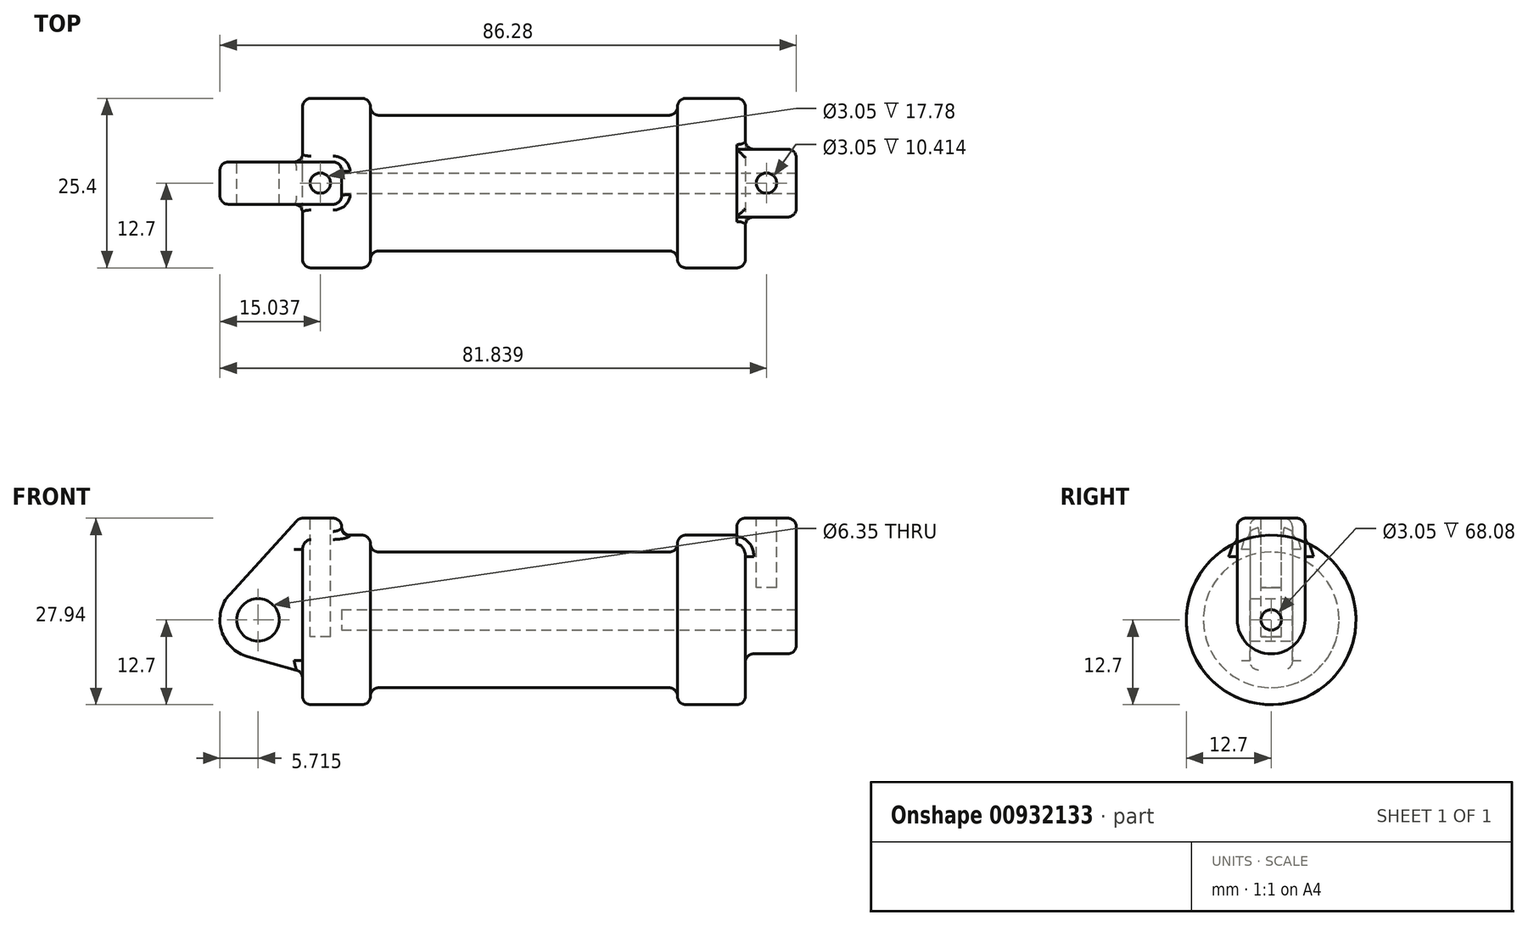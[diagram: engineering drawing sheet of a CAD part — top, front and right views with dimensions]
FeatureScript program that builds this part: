
annotation { "Feature Type Name" : "Feature", "Feature Type Description" : "" }
export const myFeature = defineFeature(function(context is Context, id is Id, definition is map)
    precondition{}
    {
        {
            var Q0;
            Q0=qCreatedBy(makeId("Front.planeOp"),FACE);
            var sketch = newSketch(context, id + "F0", { "sketchPlane" : qUnion([Q0])});
            skLineSegment(sketch, "E0", {"start": v(0, 0) * mm, "end": v(0, 12.7) * mm});
            skLineSegment(sketch, "E1", {"start": v(0, 12.7) * mm, "end": v(10.16, 12.7) * mm});
            skLineSegment(sketch, "E2", {"start": v(10.16, 12.7) * mm, "end": v(10.16, 10.16) * mm});
            skLineSegment(sketch, "E3", {"start": v(10.16, 10.16) * mm, "end": v(56.13, 10.16) * mm});
            skLineSegment(sketch, "E4", {"start": v(56.13, 10.16) * mm, "end": v(56.13, 12.7) * mm});
            skLineSegment(sketch, "E5", {"start": v(56.13, 12.7) * mm, "end": v(66.3, 12.7) * mm});
            skLineSegment(sketch, "E6", {"start": v(66.3, 12.7) * mm, "end": v(66.3, 0) * mm});
            skLineSegment(sketch, "E7", {"start": v(66.3, 0) * mm, "end": v(0, 0) * mm});
            skLineSegment(sketch, "E8", {"start": v(5.84, 15.24) * mm, "end": v(-0.5, 15.24) * mm});
            skLineSegment(sketch, "E9", {"start": v(-0.5, 15.24) * mm, "end": v(-10.88, 3.85) * mm});
            skLineSegment(sketch, "E10", {"start": v(0, 0) * mm, "end": v(-6.65, 0) * mm});
            skCircle(sketch, "E11", {"center": v(-6.65, 0) * mm, "radius": 5.72 * mm});
            skCircle(sketch, "E12", {"center": v(-6.65, 0) * mm, "radius": 3.18 * mm});
            skLineSegment(sketch, "E13", {"start": v(5.84, 15.24) * mm, "end": v(5.84, -9.4) * mm});
            skLineSegment(sketch, "E14", {"start": v(5.84, -9.4) * mm, "end": v(-8.18, -5.5) * mm});
            skLineSegment(sketch, "E15", {"start": v(5.84, 5.08) * mm, "end": v(74.63, 5.08) * mm, "construction": true});
            skSolve(sketch);
        }
        {
            var Q0;
            {var subQ0=sQuery(id+"F0.wireOp",EDGE,"E2");Q0=makeQuery(id+"F0.imprint","IMPRINT",FACE,{"disambiguationData":[TD([[makeQuery(id+"F0.imprint","IMPRINT",EDGE,{"derivedFrom":subQ0}),-1.0]])]});}
            var Q1;
            {var subQ0=sQuery(id+"F0.wireOp",EDGE,"E0");Q1=makeQuery(id+"F0.imprint","IMPRINT",FACE,{"disambiguationData":[TD([[makeQuery(id+"F0.imprint","IMPRINT",EDGE,{"derivedFrom":subQ0}),-1.0]])]});}
            var Q2;
            Q2=sQuery(id+"F0.wireOp",EDGE,"E7");
            revolve(context, id + "F1", {"surfaceOperationType" : NewSurfaceOperationType.NEW, "entities" : qUnion([Q0, Q1]), "axis" : qUnion([Q2]), "revolveType" : RevolveType.FULL});
        }
        {
            var Q0;
            {var subQ1=sQuery(id+"F0.wireOp",EDGE,"E0");Q0=makeQuery(id+"F0.imprint","IMPRINT",FACE,{"disambiguationData":[TD([[makeQuery(id+"F0.imprint","IMPRINT",EDGE,{"derivedFrom":subQ1}),1.0]])]});}
            var Q1;
            {var subQ0=sQuery(id+"F0.wireOp",EDGE,"E0");Q1=makeQuery(id+"F0.imprint","IMPRINT",FACE,{"disambiguationData":[TD([[makeQuery(id+"F0.imprint","IMPRINT",EDGE,{"derivedFrom":subQ0}),-1.0]])]});}
            var Q2;
            {var subQ0=sQuery(id+"F0.wireOp",EDGE,"E14");Q2=makeQuery(id+"F0.imprint","IMPRINT",FACE,{"disambiguationData":[TD([[makeQuery(id+"F0.imprint","IMPRINT",EDGE,{"derivedFrom":subQ0}),-1.0]])]});}
            var Q3;
            {var subQ5=sQuery(id+"F0.wireOp",EDGE,"E12");Q3=makeQuery(id+"F0.imprint","IMPRINT",FACE,{"disambiguationData":[TD([[makeQuery(id+"F0.imprint","IMPRINT",EDGE,{"derivedFrom":subQ5}),-1.0]])]});}
            extrude(context, id + "F2", {"entities" : qUnion([Q0, Q1, Q2, Q3]), "operationType" : NewBodyOperationType.ADD, "endBound" : BoundingType.SYMMETRIC, "depth" : 6.35 * mm, "offsetDistance" : 25.4 * mm});
        }
        {
            var Q0;
            Q0=makeQuery(id+"F1.opRevolve","SWEPT_FACE",FACE,{"disambiguationData":[OSD([sQuery(id+"F0.wireOp",EDGE,"E6")])]});
            var sketch = newSketch(context, id + "F3", { "sketchPlane" : qUnion([Q0])});
            skCircle(sketch, "E16", {"center": v(0, 0) * mm, "radius": 5.08 * mm});
            skCircle(sketch, "E17", {"center": v(0, 0) * mm, "radius": 1.52 * mm});
            skLineSegment(sketch, "E18", {"start": v(5.08, 0) * mm, "end": v(5.08, 15.24) * mm});
            skLineSegment(sketch, "E19", {"start": v(5.08, 15.24) * mm, "end": v(-5.08, 15.24) * mm});
            skLineSegment(sketch, "E20", {"start": v(-5.08, 15.24) * mm, "end": v(-5.08, 0) * mm});
            skSolve(sketch);
        }
        {
            var Q0;
            Q0 = qSketchRegion(id + "F3", true);
            extrude(context, id + "F4", {"entities" : qUnion([Q0]), "oppositeDirection" : true, "depth" : 1.27 * mm, "offsetDistance" : 1.27 * mm, "hasSecondDirection" : true, "secondDirectionOppositeDirection" : false, "secondDirectionDepth" : 7.62 * mm});
        }
        {
            var Q0;
            Q0=makeQuery(id+"F4.opExtrude","SWEPT_BODY",BODY,{"disambiguationData":[OSD([sQuery(id+"F3.wireOp",EDGE,"E16"),sQuery(id+"F3.wireOp",EDGE,"E17"),sQuery(id+"F3.wireOp",EDGE,"E18"),sQuery(id+"F3.wireOp",EDGE,"E19"),sQuery(id+"F3.wireOp",EDGE,"E20")])]});
            var Q1;
            Q1=makeQuery(id+"F1.opRevolve","SWEPT_BODY",BODY,{"disambiguationData":[OSD([sQuery(id+"F0.wireOp",EDGE,"E0"),sQuery(id+"F0.wireOp",EDGE,"E1"),sQuery(id+"F0.wireOp",EDGE,"E2"),sQuery(id+"F0.wireOp",EDGE,"E3"),sQuery(id+"F0.wireOp",EDGE,"E4"),sQuery(id+"F0.wireOp",EDGE,"E5"),sQuery(id+"F0.wireOp",EDGE,"E6"),sQuery(id+"F0.wireOp",EDGE,"E7")])]});
            booleanBodies(context, id + "F5", {"operationType" : BooleanOperationType.UNION, "tools" : qUnion([Q0, Q1])});
        }
        {
            var Q0;
            Q0=makeQuery(id+"F5.opBoolean","SPLIT",FACE,{"disambiguationData":[TD([makeQuery(id+"F4.opExtrude","SWEPT_FACE",FACE,{"disambiguationData":[OSD([sQuery(id+"F3.wireOp",EDGE,"E17")])]})])],"derivedFrom":makeQuery(id+"F1.opRevolve","SWEPT_FACE",FACE,{"disambiguationData":[OSD([sQuery(id+"F0.wireOp",EDGE,"E6")])]})});
            extrude(context, id + "F6", {"entities" : qUnion([Q0]), "operationType" : NewBodyOperationType.REMOVE, "oppositeDirection" : true, "depth" : 60.46 * mm, "offsetDistance" : 25.4 * mm});
        }
        {
            var Q0;
            Q0=makeQuery(id+"F4.opExtrude","SWEPT_FACE",FACE,{"disambiguationData":[OSD([sQuery(id+"F3.wireOp",EDGE,"E19")])]});
            var sketch = newSketch(context, id + "F7", { "sketchPlane" : qUnion([Q0])});
            skCircle(sketch, "E21", {"center": v(69.47, 0) * mm, "radius": 1.52 * mm});
            skPoint(sketch, "E22", {"position": v(65.02, 0) * mm});
            skLineSegment(sketch, "E23", {"start": v(65.02, -5.08) * mm, "end": v(73.91, 5.08) * mm, "construction": true});
            skLineSegment(sketch, "E24", {"start": v(65.02, 5.08) * mm, "end": v(73.91, -5.08) * mm, "construction": true});
            skSolve(sketch);
        }
        {
            var Q0;
            Q0=makeQuery(id+"F2.opExtrude","SWEPT_FACE",FACE,{"disambiguationData":[OSD([sQuery(id+"F0.wireOp",EDGE,"E8")])]});
            var sketch = newSketch(context, id + "F8", { "sketchPlane" : qUnion([Q0])});
            skCircle(sketch, "E25", {"center": v(2.67, 0) * mm, "radius": 1.52 * mm});
            skPoint(sketch, "E25.centerSnap0", {"position": v(2.67, 3.18) * mm});
            skPoint(sketch, "E25.centerSnap1", {"position": v(5.84, 0) * mm});
            skSolve(sketch);
        }
        {
            var Q0;
            Q0 = qSketchRegion(id + "F8", true);
            extrude(context, id + "F9", {"entities" : qUnion([Q0]), "operationType" : NewBodyOperationType.REMOVE, "oppositeDirection" : true, "depth" : 17.78 * mm, "offsetDistance" : 25.4 * mm});
        }
        {
            var Q0;
            Q0 = qSketchRegion(id + "F7", true);
            extrude(context, id + "F10", {"entities" : qUnion([Q0]), "operationType" : NewBodyOperationType.REMOVE, "oppositeDirection" : true, "depth" : 10.4 * mm, "offsetDistance" : 25.4 * mm});
        }
        {
            var Q0;
            Q0=makeQuery(id+"F2.opExtrude","SWEPT_FACE",FACE,{"disambiguationData":[OSD([sQuery(id+"F0.wireOp",EDGE,"E9")])]});
            var Q1;
            Q1=makeQuery(id+"F2.opExtrude","SWEPT_FACE",FACE,{"disambiguationData":[OSD([sQuery(id+"F0.wireOp",EDGE,"E13")])]});
            var Q2;
            Q2=makeQuery(id+"F2.opExtrude","CAP_EDGE",EDGE,{"disambiguationData":[OSD([sQuery(id+"F0.wireOp",EDGE,"E8")])],"isStart":true});
            var Q3;
            Q3=makeQuery(id+"F2.opExtrude","CAP_EDGE",EDGE,{"disambiguationData":[OSD([sQuery(id+"F0.wireOp",EDGE,"E8")])],"isStart":false});
            var Q4;
            Q4=makeQuery(id+"F1.opRevolve","SWEPT_FACE",FACE,{"disambiguationData":[OSD([sQuery(id+"F0.wireOp",EDGE,"E2")])]});
            var Q5;
            Q5=makeQuery(id+"F1.opRevolve","SWEPT_FACE",FACE,{"disambiguationData":[OSD([sQuery(id+"F0.wireOp",EDGE,"E0")])]});
            var Q6;
            Q6=makeQuery(id+"F1.opRevolve","SWEPT_FACE",FACE,{"disambiguationData":[OSD([sQuery(id+"F0.wireOp",EDGE,"E1")])]});
            fillet(context, id + "F11", {"entities" : qUnion([Q0, Q1, Q2, Q3, Q4, Q5, Q6]), "radius" : 1.27 * mm, "tangentPropagation" : true, "allowEdgeOverflow" : false});
        }
        {
            var Q0;
            Q0=makeQuery(id+"F1.opRevolve","SWEPT_FACE",FACE,{"disambiguationData":[OSD([sQuery(id+"F0.wireOp",EDGE,"E4")])]});
            var Q1;
            Q1=makeQuery(id+"F5.opBoolean","SPLIT",FACE,{"disambiguationData":[TD([makeQuery(id+"F1.opRevolve","SWEPT_FACE",FACE,{"disambiguationData":[OSD([sQuery(id+"F0.wireOp",EDGE,"E5")])]})])],"derivedFrom":makeQuery(id+"F1.opRevolve","SWEPT_FACE",FACE,{"disambiguationData":[OSD([sQuery(id+"F0.wireOp",EDGE,"E6")])]})});
            var Q2;
            Q2=makeQuery(id+"F4.opExtrude","CAP_EDGE",EDGE,{"disambiguationData":[OSD([sQuery(id+"F3.wireOp",EDGE,"E19")])],"isStart":true});
            var Q3;
            Q3=makeQuery(id+"F4.opExtrude","SWEPT_EDGE",EDGE,{"disambiguationData":[OSD([sQuery(id+"F3.wireOp",EDGE,"E19"),sQuery(id+"F3.wireOp",EDGE,"E20")])]});
            var Q4;
            Q4=makeQuery(id+"F4.opExtrude","CAP_EDGE",EDGE,{"disambiguationData":[OSD([sQuery(id+"F3.wireOp",EDGE,"E19")])],"isStart":false});
            var Q5;
            Q5=makeQuery(id+"F4.opExtrude","SWEPT_EDGE",EDGE,{"disambiguationData":[OSD([sQuery(id+"F3.wireOp",EDGE,"E18"),sQuery(id+"F3.wireOp",EDGE,"E19")])]});
            var Q6;
            Q6=makeQuery(id+"F4.opExtrude","CAP_EDGE",EDGE,{"disambiguationData":[OSD([sQuery(id+"F3.wireOp",EDGE,"E18")])],"isStart":true});
            fillet(context, id + "F12", {"entities" : qUnion([Q0, Q1, Q2, Q3, Q4, Q5, Q6]), "radius" : 1.27 * mm, "tangentPropagation" : true, "allowEdgeOverflow" : false});
        }
    });
